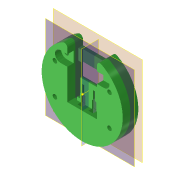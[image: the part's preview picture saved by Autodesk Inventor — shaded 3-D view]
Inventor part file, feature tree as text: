
AUTODESK INVENTOR PART (.ipt)
format: ipt  version: 2022 (Build 260153000, 153)  size: 282,112 bytes
history: native  units: in
note: dims shown in document units (in); Inventor stores cm internally (conversion verified against a paired STEP export)
features: reference x26, sketch x11, extrude x9, other x9, projected_geometry x6, plane x4, fillet x1, hole x1
ambient origin geometry x8: Origin, YZ Plane, XZ Plane, XY Plane, X Axis, Y Axis, Z Axis, Center Point
bodies: Solid1 (feature_tree)
feature tree (67):
  plane  "Work Plane1"
  extrude  "Extrusion1"  Depth=0.3937in
  other  "Arbeitspunkt1"
  plane  "Arbeitsebene4"
  extrude  "Extrusion16"  Depth=0.3937in TaperAngle=0.0deg
  extrude  "Extrusion17"  Depth=0.0394in TaperAngle=0.0deg
  extrude  "Extrusion18"  Depth=0.1181in
  extrude  "Extrusion19"  Depth=0.1181in
  extrude  "Extrusion20"  Depth=0.5512in
  extrude  "Extrusion21"  Depth=0.1575in TaperAngle=0.0deg
  extrude  "Extrusion22"  Depth=0.1102in
  fillet  "Rundung3"  Radius=0.1102in
  plane  "Arbeitsebene5"
  sketch  "Skizze29"  dims[d104=0.0in d105=0.0in d106=0.0787in]
  hole  "Bohrung2"  [1 undecoded]
  plane  "Arbeitsebene6"
  extrude  "Extrusion24"  Depth=0.0787in
  sketch  "Sketch1"  dims[d0=0.3937in d1=0.0in d17=0.7874in]
  reference  "Reference1"
  reference  "Reference5"
  reference  "Reference6"
  reference  "Reference7"
  other  "Arbeitsachse2"
  sketch  "Skizze22"  dims[d82=0.748in d84=0.3937in d85=0.0in]
  projected_geometry  "Projizierte Kontur12"
  sketch  "Skizze23"  dims[d86=0.0669in d87=0.0in d88=0.0394in d89=0.0in]
  sketch  "Skizze24"  dims[d90=0.1181in d91=0.1181in]
  sketch  "Skizze25"  dims[d92=0.1181in d93=0.1181in]
  sketch  "Skizze26"  dims[d94=0.0in d95=0.0in d96=0.5512in]
  projected_geometry  "Projizierte Kontur13"
  sketch  "Skizze27"  dims[d97=0.2756in d98=0.1575in d99=0.0in]
  projected_geometry  "Projizierte Kontur14"
  projected_geometry  "Projizierte Kontur15"
  sketch  "Skizze28"  dims[d100=0.1181in d101=0.0in d102=0.1102in d103=0.1102in]
  projected_geometry  "Projizierte Kontur16"
  sketch  "Skizze30"  dims[d107=0.1142in d108=0.2362in d109=0.1575in d110=0.0787in d111=90.0deg d112=0.2756in d113=0.8108in d116=0.0787in]
  reference  "Referenz27"
  reference  "Referenz28"
  reference  "Referenz29"
  reference  "Referenz30"
  reference  "Referenz31"
  reference  "Referenz32"
  reference  "Referenz33"
  reference  "Referenz34"
  reference  "Referenz35"
  reference  "Referenz36"
  reference  "Referenz37"
  reference  "Referenz38"
  reference  "Referenz39"
  reference  "Referenz40"
  reference  "Referenz41"
  reference  "Referenz42"
  reference  "Referenz43"
  reference  "Referenz44"
  reference  "Referenz45"
  reference  "Referenz46"
  reference  "Referenz47"
  reference  "Referenz48"
  sketch  "Skizze32"  dims[d117=0.2756in d118=0.0in]
  projected_geometry  "Projizierte Kontur18"
  other  "<userpath>\Documents\Matchboxscope\INVENTOR\Matchboxscope_v1.iam"
  other  "Matchboxscope_v1.iam"
  other  "Matchboxscope_middle2_v1:1"
  other  "Baugruppe1"
  other  "Matchboxscope_middle2_v2:1"
  other  "Assembly_USB_Lampassembly.iam"
  other  "USB_dupont_Adapter:1"
note: 1 required parameter value undecoded (feature->parameter linkage not recoverable at this tier; creation-order binding heuristic only, values carry confidence <= 0.55)
